# Revit family: Faucet-Kitchen-KOHLER-Sensate-K-72218_1
name_source: partatom
category: Plumbing Fixtures
revit_build: Autodesk Revit 2017 (Build: 20160225_1515(x64)
units: mm (PartAtom-declared; Revit-internal decimal feet)

## family parameters
Cut with Voids When Loaded = No
Host = Face
OmniClass Number = 23.31.11.00
OmniClass Title = Faucets
Part Type = Normal
Room Calculation Point = No
Round Connector Dimension = Use Diameter
Shared = No

## types (1)
- Not a Type - See Type Catalog
    ADA Compliant = Yes
    Accent Material = Default
    Apparent Load = 1800 VA
    Assembly Code = D2010
    CW Connection = Yes
    Cold Water Inlet = Cold Water Inlet
    Date Modified = 03/25/2019
    Default Elevation = 36"
    Description = Touchless kitchen faucet with 15-1/2Inch pull-down spout, DockNetik magnetic docking system and a 2-function sprayhead featuring the new Sweep spray
    Drain Included = No
    Electrical Connector = Yes
    Electrical Note = One circuit required, protected with Class A Ground-Fault Circuit-Interrupter (GFCI) or Residual Current Device (RCD)
    Faucet Hole Spacing = 0"
    Finish = Default
    Flow Rate = 2 GPM
    HW Connection = Yes
    Handle Clearance = 2 5/8"
    Height = 15 9/16"
    Hot Water Inlet = Hot Water Inlet
    Length = 8 7/16"
    Manufacturer = KOHLER Co.
    MasterFormat 1995 = 15410
    MasterFormat 2004 = 22.41.39
    Material = Premium Metal Construction
    Material_1 = Default
    Model = K-72218-CP
    Pressure = 60.00 psi
    Product Documentation Link = https://www.us.kohler.com
    Product Name = Sensate
    Product Page URL = http://www.us.kohler.com
    Spout Reach = 8 7/16"
    Type = 1
    URL = https://www.us.kohler.com
    Vent Connection = No
    Voltage = 120 V
    Waste Connection = No
    Waste Water Outlet = Waste Water Outlet
    WaterSense Certified = No
    Width = 2"

## geometry (parser evidence)
native form markers: Sweep x1
no freeform markers — native parametric forms only
